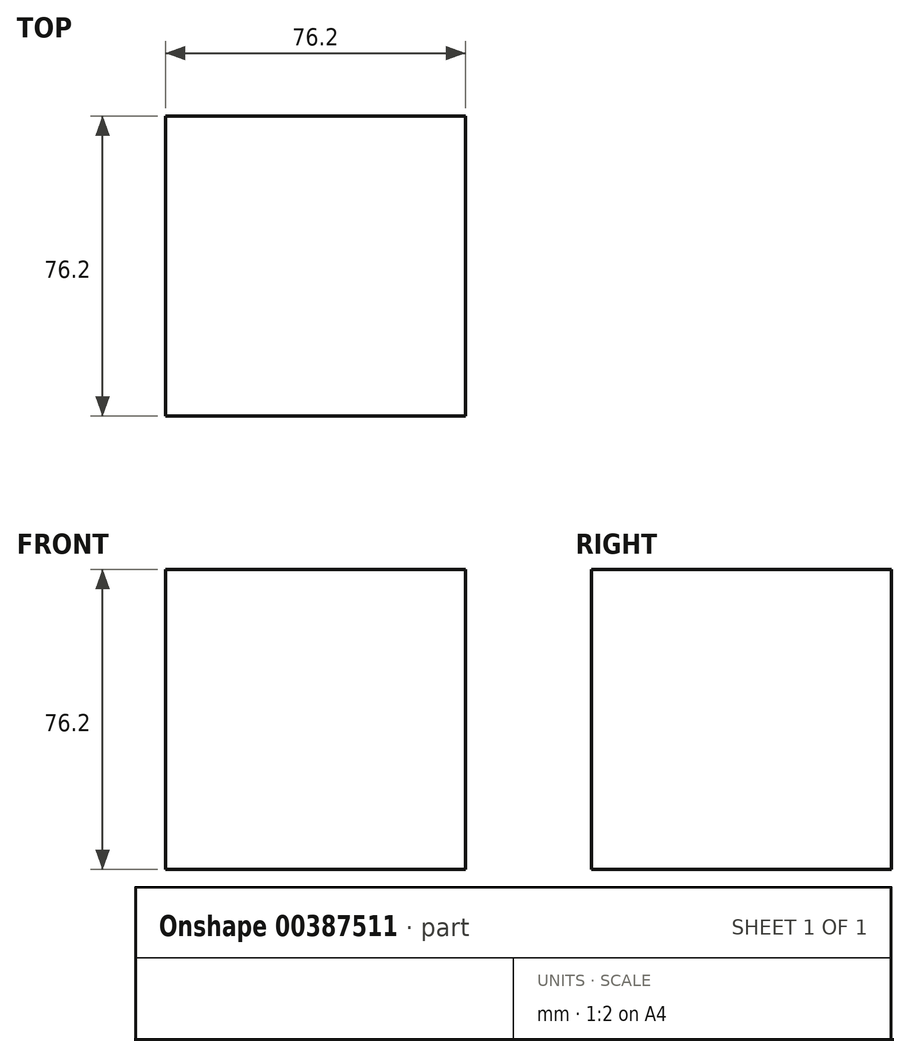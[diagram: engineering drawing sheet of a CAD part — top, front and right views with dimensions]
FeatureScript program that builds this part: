
annotation { "Feature Type Name" : "Feature", "Feature Type Description" : "" }
export const myFeature = defineFeature(function(context is Context, id is Id, definition is map)
    precondition{}
    {
        {
            var Q0;
            Q0=qCreatedBy(makeId("Front.planeOp"),FACE);
            var sketch = newSketch(context, id + "F0", { "sketchPlane" : qUnion([Q0])});
            skLineSegment(sketch, "E0.bottom", {"start": v(-119.12, 14.08) * mm, "end": v(-42.92, 14.08) * mm});
            skLineSegment(sketch, "E0.top", {"start": v(-119.12, 90.28) * mm, "end": v(-42.92, 90.28) * mm});
            skLineSegment(sketch, "E0.left", {"start": v(-119.12, 14.08) * mm, "end": v(-119.12, 90.28) * mm});
            skLineSegment(sketch, "E0.right", {"start": v(-42.92, 14.08) * mm, "end": v(-42.92, 90.28) * mm});
            skSolve(sketch);
        }
        {
            var Q0;
            Q0=makeQuery(id+"F0.imprint","IMPRINT",FACE,{"disambiguationData":[TD([[makeQuery(id+"F0.imprint","IMPRINT",EDGE,{"derivedFrom":sQuery(id+"F0.wireOp",EDGE,"E0.bottom")}),1.0]])]});
            extrude(context, id + "F1", {"entities" : qUnion([Q0]), "depth" : 76.2 * mm});
        }
    });
